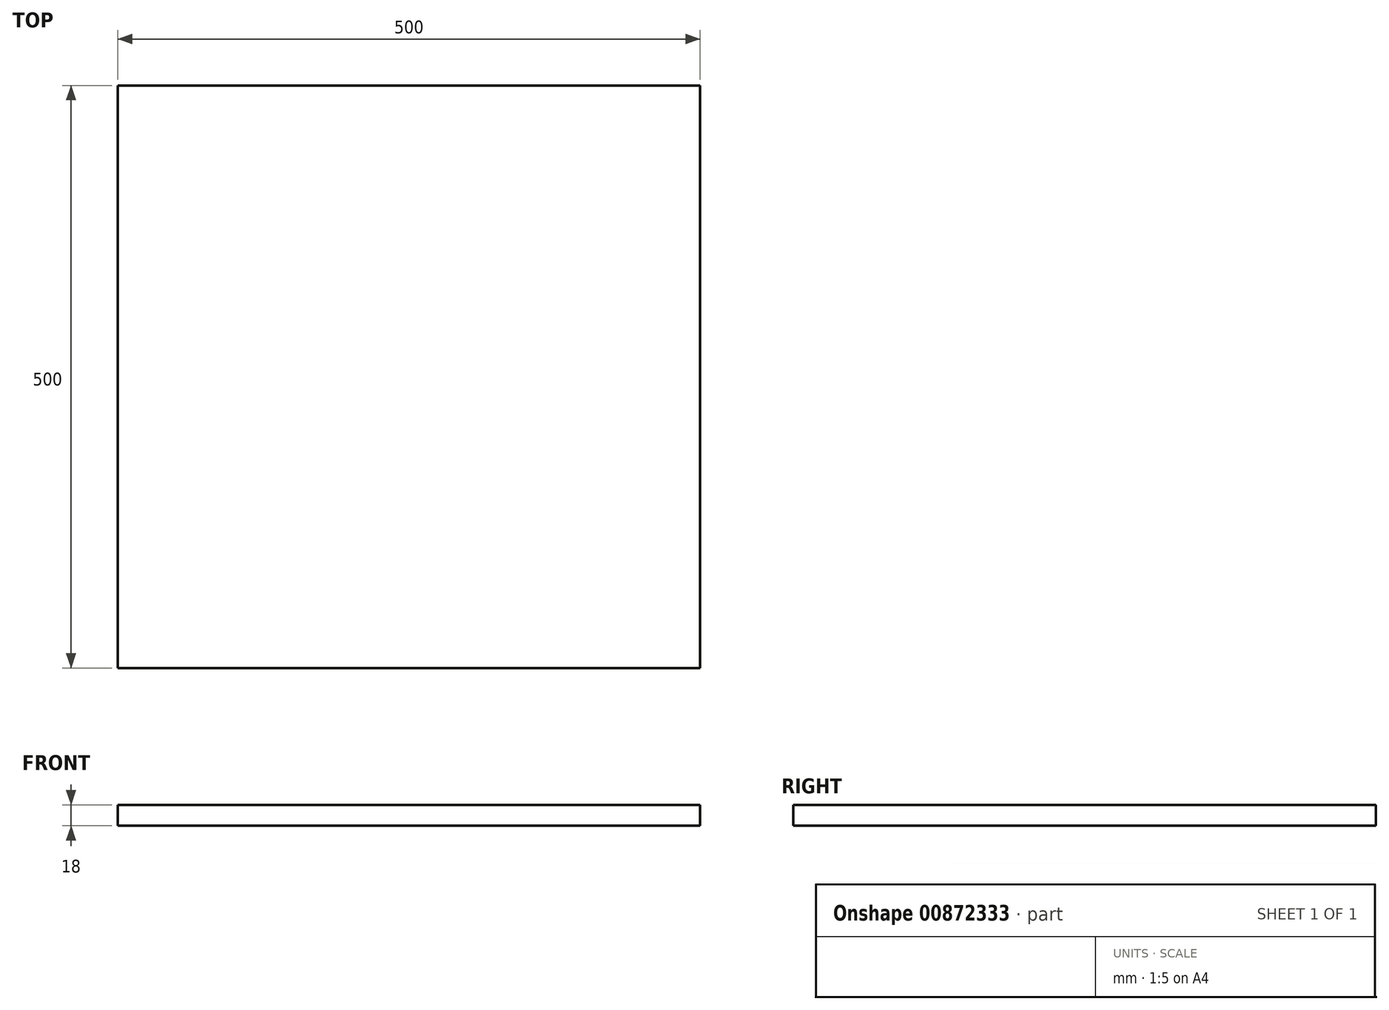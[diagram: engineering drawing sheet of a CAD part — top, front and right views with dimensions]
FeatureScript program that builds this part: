
annotation { "Feature Type Name" : "Feature", "Feature Type Description" : "" }
export const myFeature = defineFeature(function(context is Context, id is Id, definition is map)
    precondition{}
    {
        {
            var Q0;
            Q0=qCreatedBy(makeId("Front.planeOp"),FACE);
            var sketch = newSketch(context, id + "F0", { "sketchPlane" : qUnion([Q0])});
            skLineSegment(sketch, "E0.bottom", {"start": v(-250, 0) * mm, "end": v(250, 0) * mm});
            skLineSegment(sketch, "E0.top", {"start": v(-250, 18) * mm, "end": v(250, 18) * mm});
            skLineSegment(sketch, "E0.left", {"start": v(-250, 0) * mm, "end": v(-250, 18) * mm});
            skLineSegment(sketch, "E0.right", {"start": v(250, 0) * mm, "end": v(250, 18) * mm});
            skLineSegment(sketch, "E1", {"start": v(0, 0) * mm, "end": v(0, 18) * mm, "construction": true});
            skSolve(sketch);
        }
        {
            var Q0;
            Q0 = qSketchRegion(id + "F0", true);
            extrude(context, id + "F1", {"entities" : qUnion([Q0]), "depth" : 500 * mm, "offsetDistance" : 25 * mm});
        }
    });
